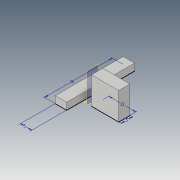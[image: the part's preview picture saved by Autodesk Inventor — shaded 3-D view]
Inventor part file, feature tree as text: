
AUTODESK INVENTOR PART (.ipt)
format: ipt  version: 2019 (Build 230136000, 136)  size: 92,672 bytes
history: native  units: mm
features: extrude x2, sketch x1, plane x1, split x1
ambient origin geometry x8: Origin, YZ Plane, XZ Plane, XY Plane, X Axis, Y Axis, Z Axis, Center Point
bodies: Solid1 (feature_tree), Solid2 (feature_tree), Solid3 (feature_tree)
feature tree (5):
  sketch  "Sketch1"  dims[d0=12.0mm d1=5.0mm d2=5.0mm d3=30.0mm d4=3.0mm d5=0.0mm d6=12.0mm d7=0.0mm d8=2.0mm]
  extrude  "Extrusion1"  Depth=5.0mm
  extrude  "Extrusion2"  Depth=5.0mm
  plane  "Work Plane1"
  split  "Split1"
